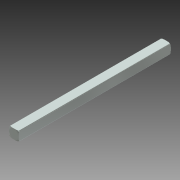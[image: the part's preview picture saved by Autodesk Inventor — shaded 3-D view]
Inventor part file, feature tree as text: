
AUTODESK INVENTOR PART (.ipt)
format: ipt  version: 2013 (Build 170138000, 138)  size: 159,744 bytes
history: native  units: in
note: dims shown in document units (in); Inventor stores cm internally (conversion verified against a paired STEP export)
features: sketch x2, plane x2, extrude x1, revolve x1, mirror x1, other x1
ambient origin geometry x8: Origin, YZ Plane, XZ Plane, XY Plane, X Axis, Y Axis, Z Axis, Center Point
bodies: Solid1 (feature_tree)
feature tree (8):
  sketch  "Sketch1"  dims[d0=2.0in d1=0.0in d2=90.0deg]
  extrude  "Extrusion1"  TaperAngle=90.0deg  [1 undecoded]
  plane  "Work Plane1"
  revolve  "Revolution1"  [1 undecoded]
  plane  "Work Plane2"
  mirror  "Mirror1"
  other  "Work Axis1"
  sketch  "Sketch2"  dims[d3=90.0deg]
note: 2 required parameter values undecoded (feature->parameter linkage not recoverable at this tier; creation-order binding heuristic only, values carry confidence <= 0.55)
